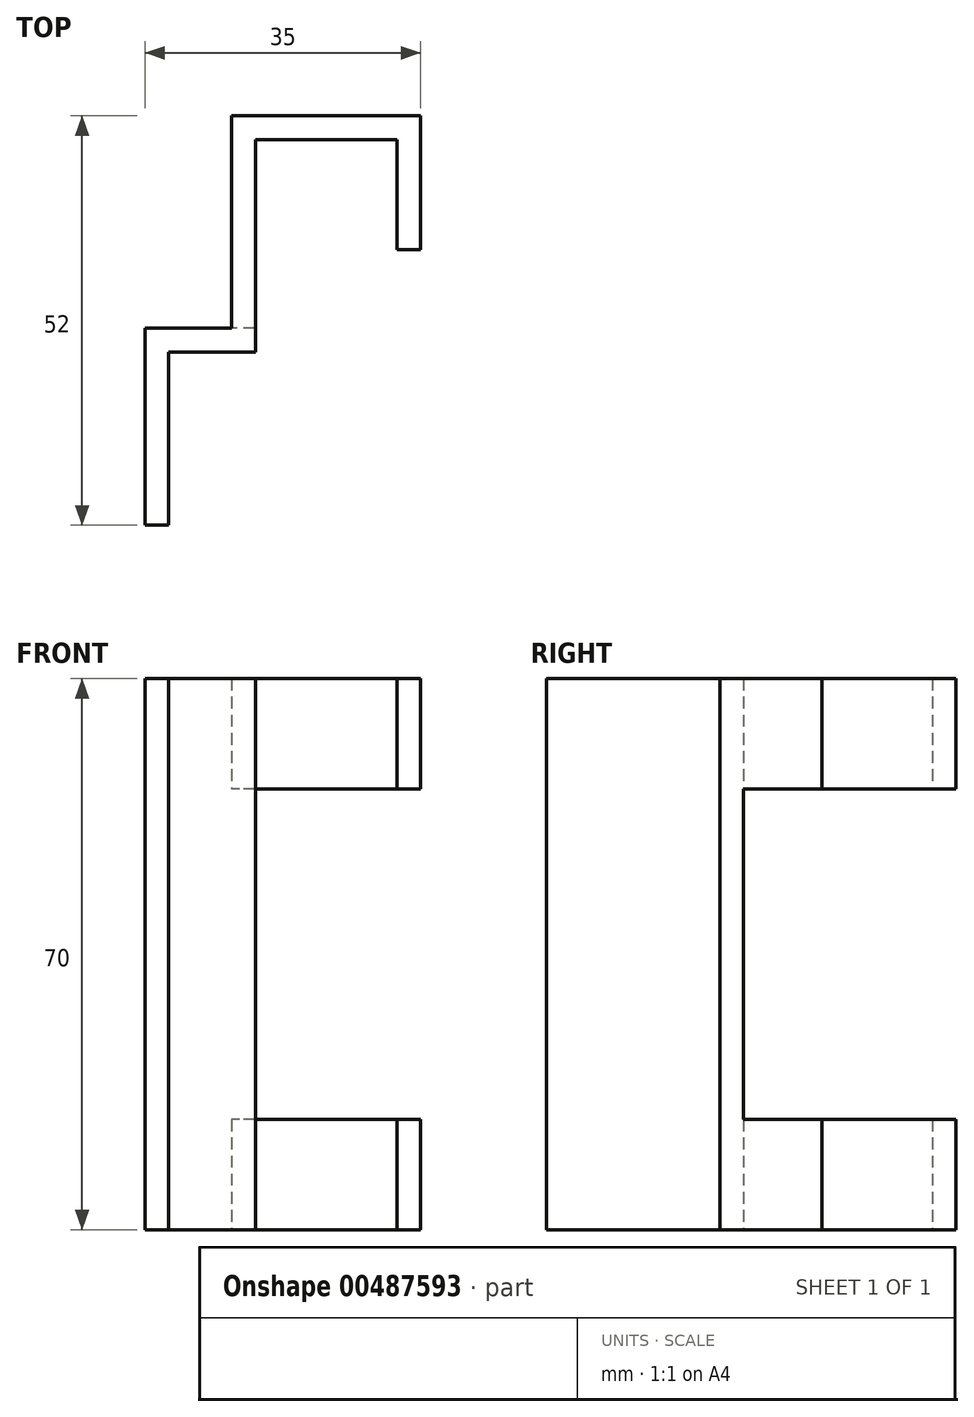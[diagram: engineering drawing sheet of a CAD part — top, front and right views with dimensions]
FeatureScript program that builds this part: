
annotation { "Feature Type Name" : "Feature", "Feature Type Description" : "" }
export const myFeature = defineFeature(function(context is Context, id is Id, definition is map)
    precondition{}
    {
        {
            var Q0;
            Q0=qCreatedBy(makeId("Top.planeOp"),FACE);
            var sketch = newSketch(context, id + "F0", { "sketchPlane" : qUnion([Q0])});
            skLineSegment(sketch, "E0", {"start": v(0, 0) * mm, "end": v(0, 14) * mm});
            skLineSegment(sketch, "E1", {"start": v(0, 14) * mm, "end": v(-18, 14) * mm});
            skLineSegment(sketch, "E2", {"start": v(-18, 14) * mm, "end": v(-18, -13) * mm});
            skLineSegment(sketch, "E3", {"start": v(-18, -13) * mm, "end": v(-29, -13) * mm});
            skLineSegment(sketch, "E4", {"start": v(-29, -13) * mm, "end": v(-29, -35) * mm});
            skLineSegment(sketch, "E5", {"start": v(0, 0) * mm, "end": v(3, 0) * mm});
            skLineSegment(sketch, "E6", {"start": v(3, 0) * mm, "end": v(3, 17) * mm});
            skLineSegment(sketch, "E7", {"start": v(3, 17) * mm, "end": v(-21, 17) * mm});
            skLineSegment(sketch, "E8", {"start": v(-21, 17) * mm, "end": v(-21, -10) * mm});
            skLineSegment(sketch, "E9", {"start": v(-21, -10) * mm, "end": v(-32, -10) * mm});
            skLineSegment(sketch, "E10", {"start": v(-32, -10) * mm, "end": v(-32, -35) * mm});
            skLineSegment(sketch, "E11", {"start": v(-32, -35) * mm, "end": v(-29, -35) * mm});
            skSolve(sketch);
        }
        {
            var Q0;
            Q0=qSketchRegion(id+"F0",true);
            extrude(context, id + "F1", {"entities" : qUnion([Q0]), "depth" : 70 * mm});
        }
        {
            var Q0;
            Q0=makeQuery(id+"F1.opExtrude","SWEPT_FACE",FACE,{"disambiguationData":[OSD([sQuery(id+"F0.wireOp",EDGE,"E8")])]});
            var sketch = newSketch(context, id + "F2", { "sketchPlane" : qUnion([Q0])});
            skLineSegment(sketch, "E12.bottom", {"start": v(-17, 14) * mm, "end": v(10, 14) * mm});
            skLineSegment(sketch, "E12.top", {"start": v(-17, 56) * mm, "end": v(10, 56) * mm});
            skLineSegment(sketch, "E12.left", {"start": v(-17, 14) * mm, "end": v(-17, 56) * mm});
            skLineSegment(sketch, "E12.right", {"start": v(10, 14) * mm, "end": v(10, 56) * mm});
            skSolve(sketch);
        }
        {
            var Q0;
            Q0 = qSketchRegion(id + "F2", true);
            extrude(context, id + "F3", {"entities" : qUnion([Q0]), "operationType" : NewBodyOperationType.REMOVE, "oppositeDirection" : true, "depth" : 25 * mm});
        }
    });
